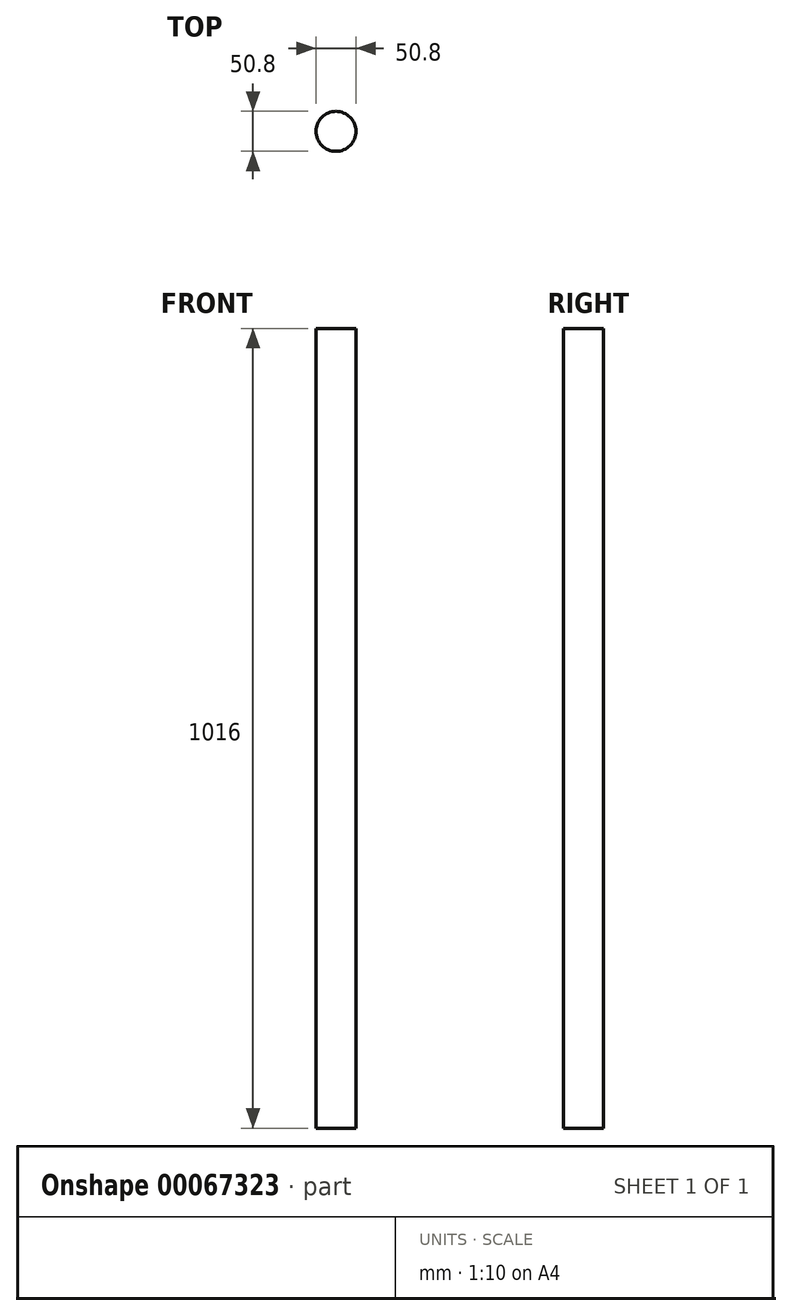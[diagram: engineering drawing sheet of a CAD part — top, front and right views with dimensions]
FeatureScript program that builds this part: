
annotation { "Feature Type Name" : "Feature", "Feature Type Description" : "" }
export const myFeature = defineFeature(function(context is Context, id is Id, definition is map)
    precondition{}
    {
        {
            var Q0;
            Q0=qCreatedBy(makeId("Top.planeOp"),FACE);
            var sketch = newSketch(context, id + "F0", { "sketchPlane" : qUnion([Q0])});
            skLineSegment(sketch, "E0", {"start": v(0, 0) * mm, "end": v(25.4, 0) * mm});
            skCircle(sketch, "E1", {"center": v(0, 0) * mm, "radius": 25.4 * mm});
            skSolve(sketch);
        }
        {
            var Q0;
            Q0 = qSketchRegion(id + "F0", true);
            extrude(context, id + "F1", {"entities" : qUnion([Q0]), "depth" : 1016 * mm});
        }
    });
